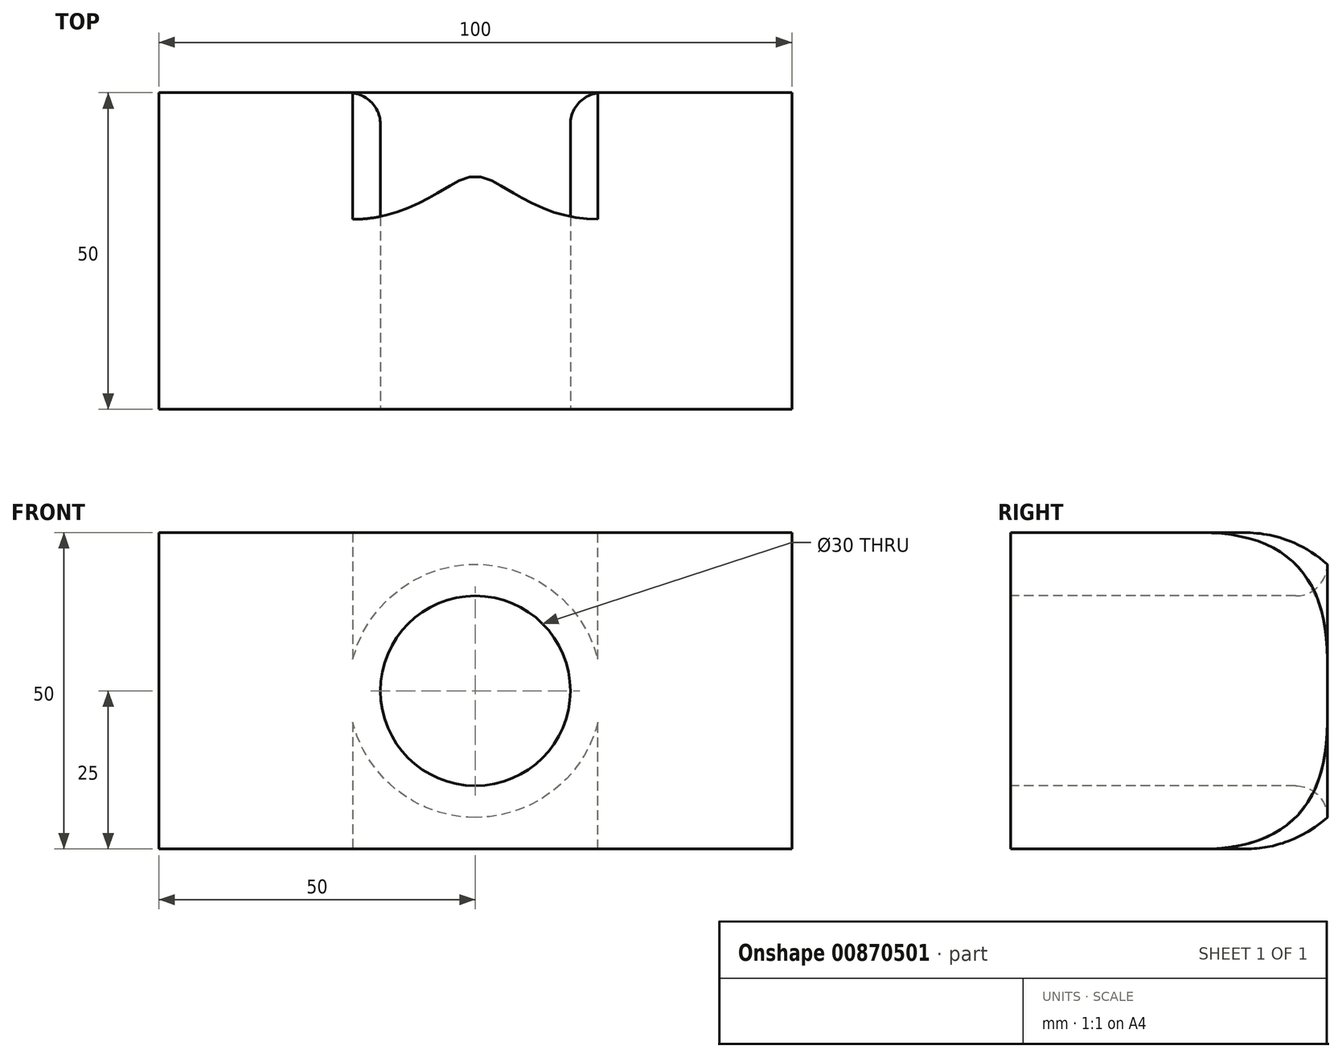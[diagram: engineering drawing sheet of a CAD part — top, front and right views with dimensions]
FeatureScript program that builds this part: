
annotation { "Feature Type Name" : "Feature", "Feature Type Description" : "" }
export const myFeature = defineFeature(function(context is Context, id is Id, definition is map)
    precondition{}
    {
        {
            var Q0;
            Q0=qCreatedBy(makeId("Front.planeOp"),FACE);
            var sketch = newSketch(context, id + "F0", { "sketchPlane" : qUnion([Q0])});
            skLineSegment(sketch, "E0.bottom", {"start": v(-50, 25) * mm, "end": v(50, 25) * mm});
            skLineSegment(sketch, "E0.top", {"start": v(-50, -25) * mm, "end": v(50, -25) * mm});
            skLineSegment(sketch, "E0.left", {"start": v(-50, 25) * mm, "end": v(-50, -25) * mm});
            skLineSegment(sketch, "E0.right", {"start": v(50, 25) * mm, "end": v(50, -25) * mm});
            skPoint(sketch, "E0.middle", {"position": v(0, 0) * mm});
            skSolve(sketch);
        }
        {
            var Q0;
            Q0 = qSketchRegion(id + "F0", true);
            extrude(context, id + "F1", {"entities" : qUnion([Q0]), "endBound" : BoundingType.SYMMETRIC, "depth" : 50 * mm, "offsetDistance" : 25 * mm});
        }
        {
            var Q0;
            Q0=makeQuery(id+"F1.opExtrude","CAP_FACE",FACE,{"disambiguationData":[OSD([sQuery(id+"F0.wireOp",EDGE,"E0.bottom"),sQuery(id+"F0.wireOp",EDGE,"E0.top"),sQuery(id+"F0.wireOp",EDGE,"E0.left"),sQuery(id+"F0.wireOp",EDGE,"E0.right")])],"isStart":false});
            var sketch = newSketch(context, id + "F2", { "sketchPlane" : qUnion([Q0])});
            skCircle(sketch, "E1", {"center": v(0, 0) * mm, "radius": 15 * mm});
            skSolve(sketch);
        }
        {
            var Q0;
            Q0 = qSketchRegion(id + "F2", true);
            extrude(context, id + "F3", {"entities" : qUnion([Q0]), "operationType" : NewBodyOperationType.REMOVE, "endBound" : BoundingType.THROUGH_ALL, "oppositeDirection" : true, "depth" : 25 * mm, "offsetDistance" : 25 * mm});
        }
        {
            var Q0;
            Q0=makeQuery(id+"F3.boolean.opBoolean","COPY",EDGE,{"derivedFrom":makeQuery(id+"F3.opExtrude","CAP_EDGE",EDGE,{"disambiguationData":[OSD([sQuery(id+"F2.wireOp",EDGE,"E1")])],"isStart":true})});
            var Q1;
            Q1=makeQuery(id+"F3.boolean.opBoolean","INTERSECT",EDGE,{"derivedFrom":[makeQuery(id+"F1.opExtrude","CAP_FACE",FACE,{"disambiguationData":[OSD([sQuery(id+"F0.wireOp",EDGE,"E0.bottom"),sQuery(id+"F0.wireOp",EDGE,"E0.top"),sQuery(id+"F0.wireOp",EDGE,"E0.left"),sQuery(id+"F0.wireOp",EDGE,"E0.right")])],"isStart":true}),makeQuery(id+"F3.opExtrude","SWEPT_FACE",FACE,{"disambiguationData":[OSD([sQuery(id+"F2.wireOp",EDGE,"E1")])]})]});
            fillet(context, id + "F4", {"entities" : qUnion([Q0, Q1]), "radius" : 5 * mm, "tangentPropagation" : true, "allowEdgeOverflow" : false});
        }
        {
            var Q0;
            Q0=qCreatedBy(makeId("Top.planeOp"),FACE);
            var Q1;
            Q1=makeQuery(id+"F1.opExtrude","SWEPT_EDGE",EDGE,{"disambiguationData":[OSD([sQuery(id+"F0.wireOp",EDGE,"E0.bottom"),sQuery(id+"F0.wireOp",EDGE,"E0.left")])]});
            cPlane(context, id + "F5", {"entities" : qUnion([Q0, Q1]), "cplaneType" : CPlaneType.LINE_ANGLE, "offset" : 25 * mm, "angle" : 45 * degree, "width" : 150 * mm, "height" : 150 * mm});
        }
        {
            var Q0;
            Q0=qCreatedBy(id+"F5.planeOp",FACE);
            var sketch = newSketch(context, id + "F6", { "sketchPlane" : qUnion([Q0])});
            skCircle(sketch, "E2", {"center": v(-53.03, 0) * mm, "radius": 15 * mm});
            skSolve(sketch);
        }
        {
            var Q0;
            Q0 = qSketchRegion(id + "F6", true);
            extrude(context, id + "F7", {"entities" : qUnion([Q0]), "operationType" : NewBodyOperationType.REMOVE, "endBound" : BoundingType.SYMMETRIC, "oppositeDirection" : true, "depth" : 60 * mm, "offsetDistance" : 25 * mm});
        }
        {
            var Q0;
            Q0=makeQuery(id+"F1.opExtrude","CAP_EDGE",EDGE,{"disambiguationData":[OSD([sQuery(id+"F0.wireOp",EDGE,"E0.top")])],"isStart":true});
            var Q1;
            Q1=makeQuery(id+"F1.opExtrude","CAP_EDGE",EDGE,{"disambiguationData":[OSD([sQuery(id+"F0.wireOp",EDGE,"E0.bottom")])],"isStart":true});
            fillet(context, id + "F8", {"entities" : qUnion([Q0, Q1]), "radius" : 20 * mm, "tangentPropagation" : true, "rho" : 0.5, "crossSection" : FilletCrossSection.CONIC, "allowEdgeOverflow" : false});
        }
    });
